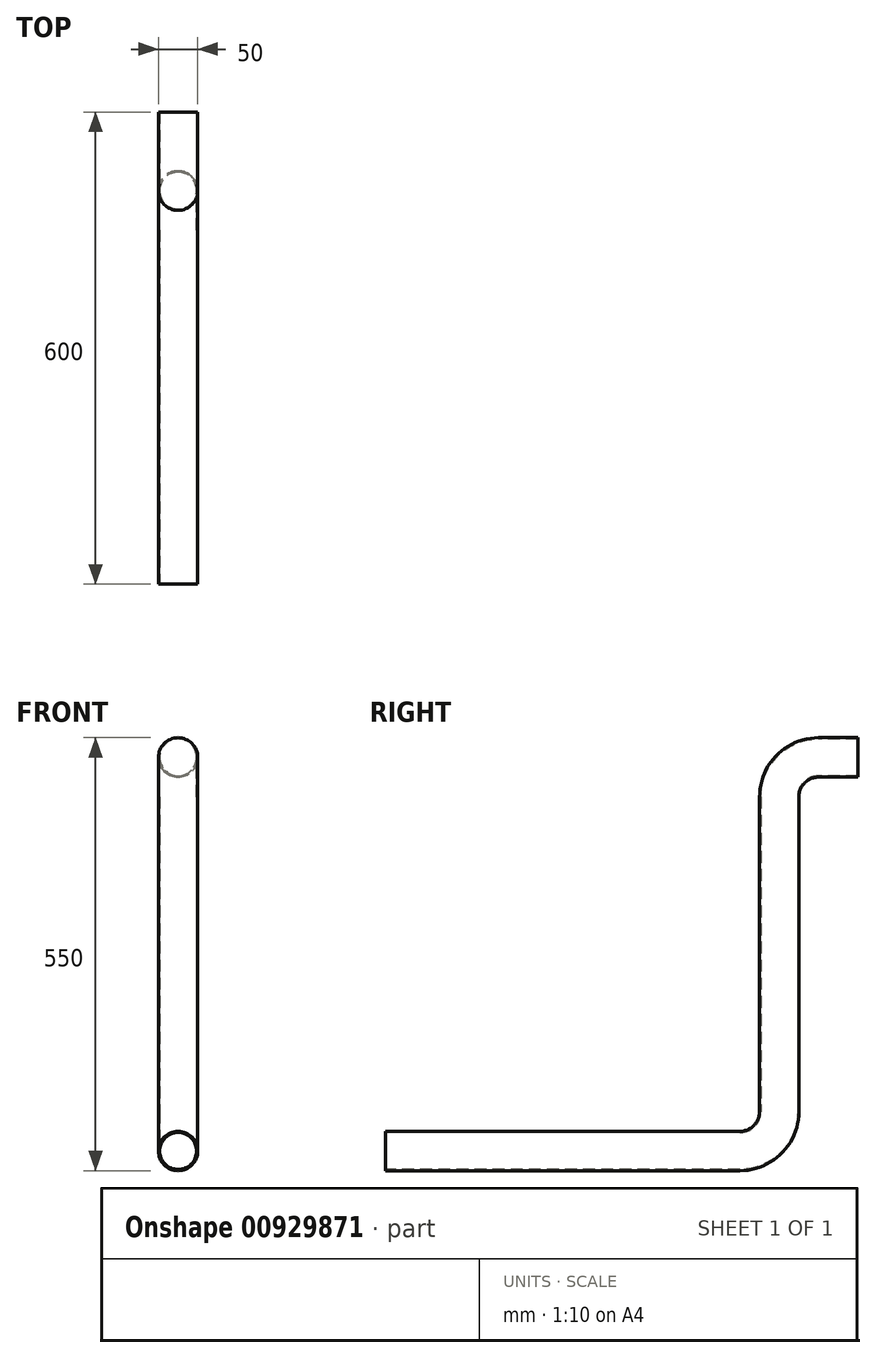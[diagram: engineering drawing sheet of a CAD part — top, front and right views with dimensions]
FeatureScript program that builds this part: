
annotation { "Feature Type Name" : "Feature", "Feature Type Description" : "" }
export const myFeature = defineFeature(function(context is Context, id is Id, definition is map)
    precondition{}
    {
        {
            var Q0;
            Q0=qCreatedBy(makeId("Front.planeOp"),FACE);
            var sketch = newSketch(context, id + "F0", { "sketchPlane" : qUnion([Q0])});
            skCircle(sketch, "E0", {"center": v(0, 0) * mm, "radius": 25 * mm});
            skCircle(sketch, "E1", {"center": v(0, 0) * mm, "radius": 23.5 * mm});
            skSolve(sketch);
        }
        {
            var Q0;
            Q0=qCreatedBy(makeId("Right.planeOp"),FACE);
            var sketch = newSketch(context, id + "F1", { "sketchPlane" : qUnion([Q0])});
            skLineSegment(sketch, "E2", {"start": v(0, 0) * mm, "end": v(-50, 0) * mm});
            skLineSegment(sketch, "E3", {"start": v(-100, -50) * mm, "end": v(-100, -450) * mm});
            skLineSegment(sketch, "E4", {"start": v(-150, -500) * mm, "end": v(-600, -500) * mm});
            skPoint(sketch, "E5.visualSharp", {"position": v(-100, 0) * mm});
            skArc(sketch, "E5.filletArc", {"start": v(-50, 0) * mm, "mid": v(-85.36, -14.64) * mm, "end": v(-100, -50) * mm});
            skPoint(sketch, "E6.visualSharp", {"position": v(-100, -500) * mm});
            skArc(sketch, "E6.filletArc", {"start": v(-150, -500) * mm, "mid": v(-114.64, -485.36) * mm, "end": v(-100, -450) * mm});
            skSolve(sketch);
        }
        {
            var Q0;
            Q0=makeQuery(id+"F0.imprint","IMPRINT",FACE,{"disambiguationData":[TD([[makeQuery(id+"F0.imprint","IMPRINT",EDGE,{"derivedFrom":sQuery(id+"F0.wireOp",EDGE,"E0")}),1.0]])]});
            var Q1;
            Q1=sQuery(id+"F1.wireOp",EDGE,"E2");
            var Q2;
            Q2=sQuery(id+"F1.wireOp",EDGE,"E5.filletArc");
            var Q3;
            Q3=sQuery(id+"F1.wireOp",EDGE,"E3");
            var Q4;
            Q4=sQuery(id+"F1.wireOp",EDGE,"E6.filletArc");
            var Q5;
            Q5=sQuery(id+"F1.wireOp",EDGE,"E4");
            sweep(context, id + "F2", {"profiles" : qUnion([Q0]), "path" : qUnion([Q1, Q2, Q3, Q4, Q5])});
        }
    });
